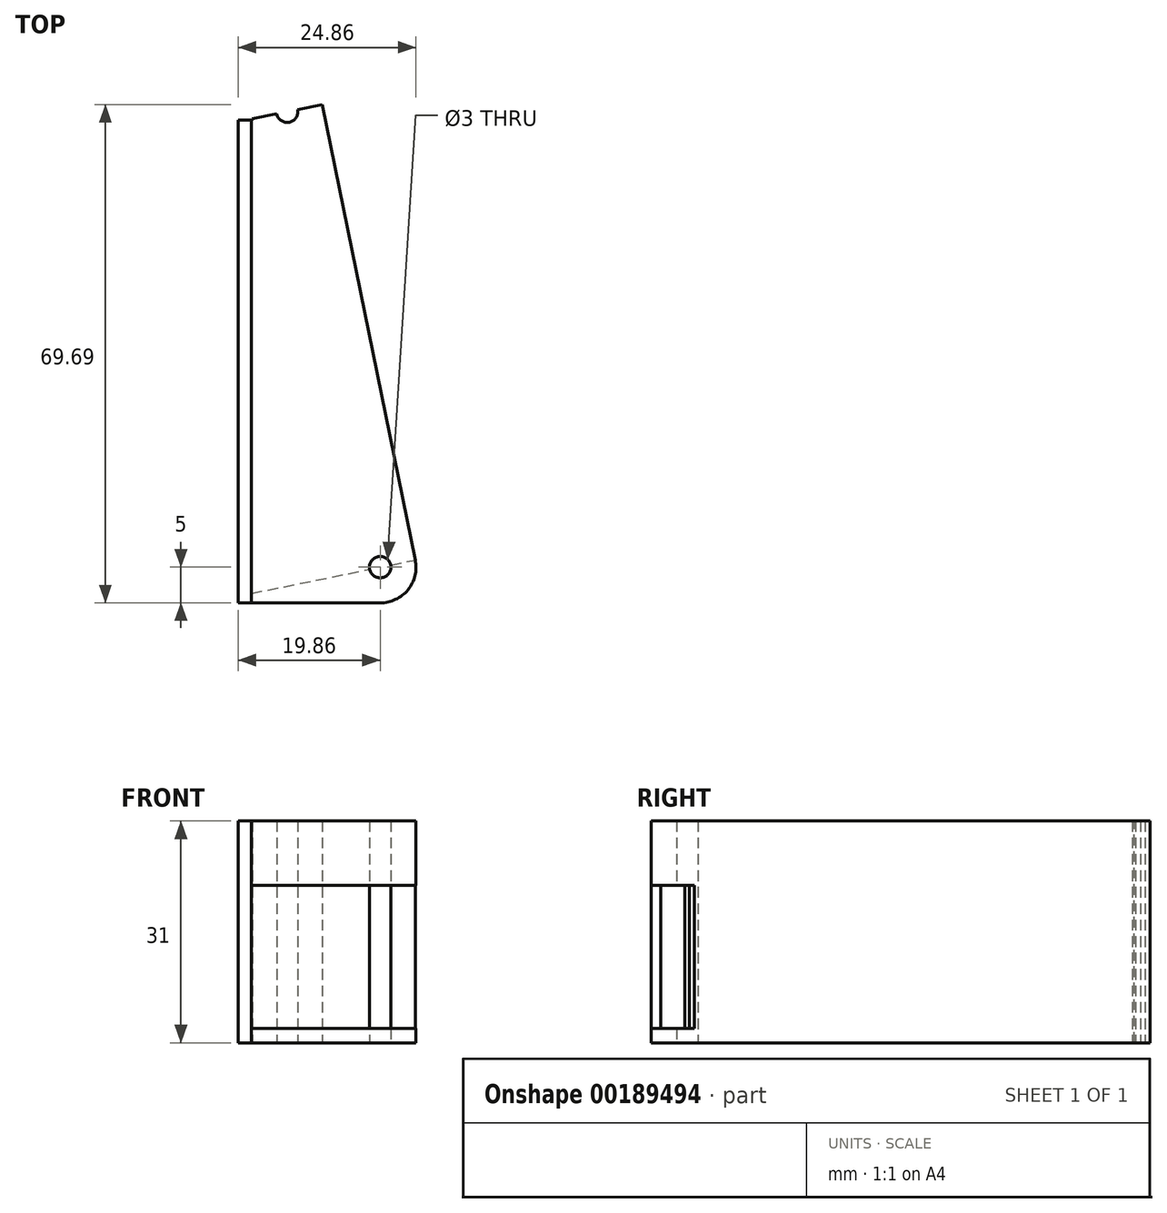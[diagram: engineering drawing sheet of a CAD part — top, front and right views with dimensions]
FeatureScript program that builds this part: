
annotation { "Feature Type Name" : "Feature", "Feature Type Description" : "" }
export const myFeature = defineFeature(function(context is Context, id is Id, definition is map)
    precondition{}
    {
        {
            var Q0;
            Q0=qCreatedBy(makeId("Top.planeOp"),FACE);
            var sketch = newSketch(context, id + "F0", { "sketchPlane" : qUnion([Q0])});
            skCircle(sketch, "E0", {"center": v(0, 0) * mm, "radius": 1.5 * mm});
            skArc(sketch, "E1", {"start": v(0, -5) * mm, "mid": v(3.87, -3.16) * mm, "end": v(4.9, 1) * mm});
            skLineSegment(sketch, "E2", {"start": v(0, 0) * mm, "end": v(-1.5, 0) * mm});
            skCircle(sketch, "E3", {"center": v(-13, 63.69) * mm, "radius": 1.5 * mm});
            skArc(sketch, "E4", {"start": v(-8.1, 64.69) * mm, "mid": v(-14.1, 68.57) * mm, "end": v(-17.86, 62.5) * mm});
            skLineSegment(sketch, "E5", {"start": v(-13, 63.69) * mm, "end": v(-18, 63.69) * mm});
            skLineSegment(sketch, "E6", {"start": v(-18, 63.69) * mm, "end": v(-18, -5) * mm});
            skLineSegment(sketch, "E7", {"start": v(0, 0) * mm, "end": v(0, -5) * mm});
            skLineSegment(sketch, "E8", {"start": v(0, -5) * mm, "end": v(-18, -5) * mm});
            skArc(sketch, "E9.trimOffspring", {"start": v(-17.86, 62.5) * mm, "mid": v(-17.93, 62.48) * mm, "end": v(-18, 62.46) * mm});
            skLineSegment(sketch, "E10", {"start": v(4.9, 1) * mm, "end": v(-8.1, 64.69) * mm});
            skSolve(sketch);
        }
        {
            var Q0;
            Q0=makeQuery(id+"F0.imprint","IMPRINT",FACE,{"disambiguationData":[TD([[makeQuery(id+"F0.imprint","IMPRINT",EDGE,{"derivedFrom":sQuery(id+"F0.wireOp",EDGE,"E1")}),1.0]])]});
            extrude(context, id + "F1", {"entities" : qUnion([Q0]), "depth" : 31 * mm});
        }
        {
            var Q0;
            Q0=makeQuery(id+"F1.opExtrude","SWEPT_FACE",FACE,{"disambiguationData":[OSD([sQuery(id+"F0.wireOp",EDGE,"E10")])]});
            var sketch = newSketch(context, id + "F2", { "sketchPlane" : qUnion([Q0])});
            skLineSegment(sketch, "E11.0.0", {"start": v(0, 0) * mm, "end": v(65, 0) * mm});
            skLineSegment(sketch, "E11.0.2", {"start": v(65, 31) * mm, "end": v(0, 31) * mm});
            skLineSegment(sketch, "E11.0.3", {"start": v(0, 31) * mm, "end": v(0, 29) * mm});
            skLineSegment(sketch, "E12", {"start": v(70, 31) * mm, "end": v(70, 0) * mm});
            skLineSegment(sketch, "E13", {"start": v(70, 0) * mm, "end": v(-5, 0) * mm});
            skLineSegment(sketch, "E14", {"start": v(70, 31) * mm, "end": v(-5, 31) * mm});
            skLineSegment(sketch, "E15", {"start": v(70, 0) * mm, "end": v(70, 2) * mm});
            skLineSegment(sketch, "E16", {"start": v(70, 2) * mm, "end": v(-5, 2) * mm});
            skLineSegment(sketch, "E17", {"start": v(70, 31) * mm, "end": v(70, 29) * mm});
            skLineSegment(sketch, "E18", {"start": v(-5, 31) * mm, "end": v(-5, 0) * mm});
            skLineSegment(sketch, "E19", {"start": v(70, 29) * mm, "end": v(-5, 29) * mm});
            skLineSegment(sketch, "E20", {"start": v(70, 29) * mm, "end": v(70, 22) * mm});
            skLineSegment(sketch, "E21", {"start": v(70, 22) * mm, "end": v(50, 22) * mm});
            skLineSegment(sketch, "E22", {"start": v(50, 22) * mm, "end": v(50, 29) * mm});
            skLineSegment(sketch, "E23", {"start": v(-5, 22) * mm, "end": v(10, 22) * mm});
            skLineSegment(sketch, "E24", {"start": v(10, 22) * mm, "end": v(10, 29) * mm});
            skLineSegment(sketch, "E25.trimOffspring", {"start": v(10, 22) * mm, "end": v(-5, 22) * mm});
            skLineSegment(sketch, "E26", {"start": v(70, 2) * mm, "end": v(70, 12) * mm});
            skLineSegment(sketch, "E27", {"start": v(70, 12) * mm, "end": v(45, 12) * mm});
            skLineSegment(sketch, "E28", {"start": v(45, 12) * mm, "end": v(45, 2) * mm});
            skSolve(sketch);
        }
        {
            var Q0;
            {var subQ0=sQuery(id+"F2.wireOp",EDGE,"E22");Q0=makeQuery(id+"F2.imprint","IMPRINT",FACE,{"disambiguationData":[TD([[makeQuery(id+"F2.imprint","IMPRINT",EDGE,{"derivedFrom":subQ0}),1.0]])]});}
            var Q1;
            {var subQ0=sQuery(id+"F2.wireOp",EDGE,"E12");Q1=makeQuery(id+"F2.imprint","IMPRINT",FACE,{"disambiguationData":[TD([[makeQuery(id+"F2.imprint","IMPRINT",EDGE,{"derivedFrom":subQ0}),-1.0]])]});}
            var Q2;
            {var subQ0=sQuery(id+"F2.wireOp",EDGE,"E18");var subQ1=sQuery(id+"F2.wireOp",EDGE,"E16");var subQ2=makeQuery(id+"F2.imprint","INTERSECT",VERTEX,{"derivedFrom":[subQ1,subQ0]});Q2=makeQuery(id+"F2.imprint","IMPRINT",FACE,{"disambiguationData":[TD([[makeQuery(id+"F2.imprint","IMPRINT",EDGE,{"disambiguationData":[TD([[subQ2,1.0]])],"derivedFrom":subQ0}),1.0]])]});}
            extrude(context, id + "F3", {"entities" : qUnion([Q0, Q1, Q2]), "operationType" : NewBodyOperationType.REMOVE, "oppositeDirection" : true, "depth" : 25 * mm});
        }
        {
            var Q0;
            Q0=makeQuery(id+"F1.opExtrude","CAP_FACE",FACE,{"disambiguationData":[OSD([sQuery(id+"F0.wireOp",EDGE,"E0"),sQuery(id+"F0.wireOp",EDGE,"E1"),sQuery(id+"F0.wireOp",EDGE,"E3"),sQuery(id+"F0.wireOp",EDGE,"E4"),sQuery(id+"F0.wireOp",EDGE,"E6"),sQuery(id+"F0.wireOp",EDGE,"E8"),sQuery(id+"F0.wireOp",EDGE,"E9.trimOffspring"),sQuery(id+"F0.wireOp",EDGE,"E10")])],"isStart":false});
            var sketch = newSketch(context, id + "F4", { "sketchPlane" : qUnion([Q0])});
            skArc(sketch, "E29.0.0", {"start": v(-8.1, 64.69) * mm, "mid": v(-14.1, 68.57) * mm, "end": v(-17.86, 62.5) * mm});
            skArc(sketch, "E29.0.1", {"start": v(-17.86, 62.5) * mm, "mid": v(-17.93, 62.48) * mm, "end": v(-18, 62.46) * mm});
            skLineSegment(sketch, "E29.0.2", {"start": v(-18, 62.46) * mm, "end": v(-18, -5) * mm});
            skLineSegment(sketch, "E29.0.3", {"start": v(-18, -5) * mm, "end": v(0, -5) * mm});
            skArc(sketch, "E29.0.4", {"start": v(0, -5) * mm, "mid": v(3.87, -3.16) * mm, "end": v(4.9, 1) * mm});
            skLineSegment(sketch, "E29.0.5", {"start": v(4.9, 1) * mm, "end": v(-8.1, 64.69) * mm});
            skLineSegment(sketch, "E30.bottom", {"start": v(-17.86, 62.5) * mm, "end": v(-19.86, 62.5) * mm});
            skLineSegment(sketch, "E30.top", {"start": v(-17.86, -5) * mm, "end": v(-19.86, -5) * mm});
            skLineSegment(sketch, "E30.left", {"start": v(-17.86, 62.5) * mm, "end": v(-17.86, -5) * mm});
            skLineSegment(sketch, "E30.right", {"start": v(-19.86, 62.5) * mm, "end": v(-19.86, -5) * mm});
            skSolve(sketch);
        }
        {
            var Q0;
            Q0=makeQuery(id+"F4.imprint","IMPRINT",FACE,{"disambiguationData":[TD([[makeQuery(id+"F4.imprint","IMPRINT",EDGE,{"derivedFrom":sQuery(id+"F4.wireOp",EDGE,"E29.0.1")}),-1.0]])]});
            extrude(context, id + "F5", {"entities" : qUnion([Q0]), "oppositeDirection" : true, "depth" : 31 * mm});
        }
        {
            var Q0;
            Q0=makeQuery(id+"F4.imprint","IMPRINT",FACE,{"disambiguationData":[TD([[makeQuery(id+"F4.imprint","IMPRINT",EDGE,{"derivedFrom":sQuery(id+"F4.wireOp",EDGE,"E29.0.0")}),1.0]])]});
            var sketch = newSketch(context, id + "F6", { "sketchPlane" : qUnion([Q0])});
            skCircle(sketch, "E31.0", {"center": v(-13, 63.69) * mm, "radius": 1.5 * mm});
            skPoint(sketch, "E32.0", {"position": v(-14.1, 68.57) * mm});
            skArc(sketch, "E33.0", {"start": v(-8.1, 64.69) * mm, "mid": v(-14.1, 68.57) * mm, "end": v(-17.86, 62.5) * mm});
            skCircle(sketch, "E34", {"center": v(-13, 63.69) * mm, "radius": 5 * mm});
            skSolve(sketch);
        }
        {
            var Q0;
            Q0=makeQuery(id+"F6.imprint","IMPRINT",FACE,{"disambiguationData":[TD([[makeQuery(id+"F6.imprint","IMPRINT",EDGE,{"derivedFrom":sQuery(id+"F6.wireOp",EDGE,"E31.0")}),-1.0]])]});
            extrude(context, id + "F7", {"entities" : qUnion([Q0]), "operationType" : NewBodyOperationType.REMOVE, "oppositeDirection" : true, "depth" : 3 * mm});
        }
    });
